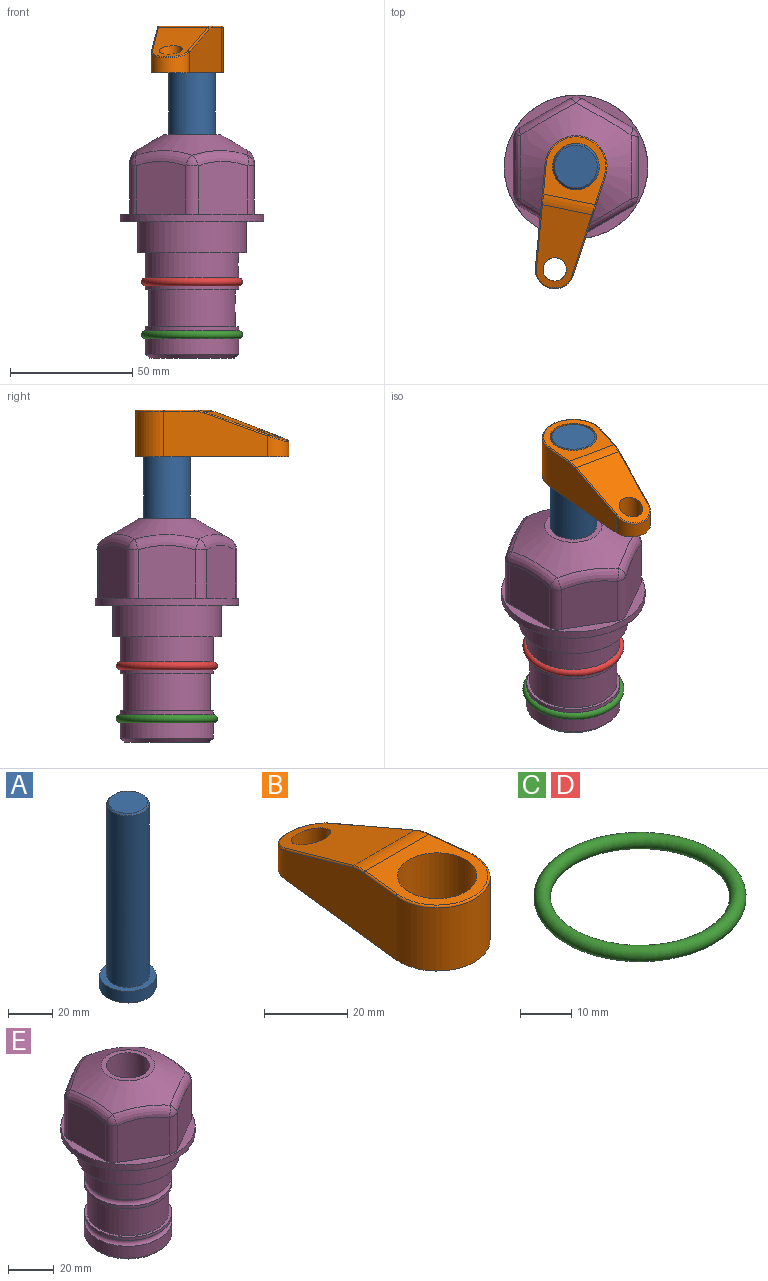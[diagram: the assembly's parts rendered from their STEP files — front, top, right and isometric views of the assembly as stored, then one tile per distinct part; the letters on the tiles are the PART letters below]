
ASSEMBLY  parts=5 mates=3
PART A: 6 faces, bbox 25.4x25.4x101.6 mm
  f0: plane 17.46x17.46mm, normal (0,0,1), area 239.5mm2, adj f5
  f1: plane 25.4x25.4mm, normal (0,0,-1), area 506.7mm2, adj f2
  f2: cylinder r=12.7mm len=25.4mm, axis (0,0,1), area 506.7mm2, adj f1,f3
  f3: plane 25.4x25.4mm, normal (0,0,1), area 221.7mm2, adj f2,f4
  f4: cylinder r=9.53mm len=94.46mm, axis (0,0,1), area 5653mm2, adj f3,f5
  f5: cone r=8.73mm half-angle=45deg, axis (0,0,-1), area 64.4mm2, adj f0,f4
PART B: 44 faces, bbox 27.5x64.5x19.1 mm
  f0: plane 2.3x0.95mm, normal (0,0,-1), area 1mm2, adj f25,f30,f34
  f1: plane 63.5x25.4mm, normal (0,0,-1), area 561.7mm2, adj f2,f3,f4,f5,f6,f7,f19,f20
  f2: cylinder r=12.7mm len=25.4mm, axis (0,0,-1), area 792.2mm2, adj f1,f3,f5,f13
  f3: plane 42.33x18.54mm, normal (0.99,0.11,0), area 647mm2, adj f1,f2,f4,f11,f12,f14
  f4: cylinder r=7.94mm len=15.78mm, axis (0,0,-1), area 158.6mm2, adj f1,f3,f5,f16
  f5: plane 42.33x18.54mm, normal (-0.99,0.11,0), area 647mm2, adj f1,f2,f4,f15,f17,f18
  f6: cylinder r=9.53mm len=19.05mm, axis (0,0,-1), area 1140.1mm2, adj f1,f8
  f7: cylinder r=4.76mm len=10.98mm, axis (0,0,-1), area 276.1mm2, adj f1,f9
  f8: plane 25.83x24.38mm, normal (0,0,1), area 262.2mm2, adj f6,f10,f11,f13,f15
  f9: plane 32.49x20.55mm, normal (0,0.34,0.94), area 489.9mm2, adj f7,f10,f14,f16,f18
  f10: cylinder r=12.7mm len=21.49mm, axis (-1,0,0), area 93.2mm2, adj f8,f9,f12,f17
  f11: cylinder r=0.51mm len=12.34mm, axis (0.11,-0.99,0), area 9.9mm2, adj f3,f8,f12,f13
  f12: bspline ~7.62x1.64mm, area 3.5mm2, adj f3,f10,f11,f14
  f13: torus R=12.19mm, axis (0,0,1), area 33.6mm2, adj f2,f8,f11,f15
  f14: cylinder r=0.51mm len=26.01mm, axis (0.1,-0.93,0.34), area 21.6mm2, adj f3,f9,f12,f16
  f15: cylinder r=0.51mm len=12.34mm, axis (0.11,0.99,0), area 9.9mm2, adj f5,f8,f13,f17
  f16: bspline ~15.78x7.05mm, area 15.7mm2, adj f4,f9,f14,f18
  f17: bspline ~7.62x1.64mm, area 3.5mm2, adj f5,f10,f15,f18
  f18: cylinder r=0.51mm len=26.01mm, axis (0.1,0.93,-0.34), area 21.6mm2, adj f5,f9,f16,f17
  f19: plane 21.6x14.29mm, normal (-0.99,-0.11,0), area 242.6mm2, adj f1,f26,f28,f34,f36,f38
  f20: plane 21.6x14.29mm, normal (0.99,-0.11,0), area 242.6mm2, adj f1,f27,f29,f37,f39,f41
  f21: cylinder r=12.7mm len=14.29mm, axis (0,0,-1), area 173.2mm2, adj f1,f26,f27,f30,f31,f33
  f22: cylinder r=7.94mm len=7.63mm, axis (0,0,-1), area 53.8mm2, adj f1,f28,f29,f42
  f23: plane 2.3x0.95mm, normal (0,0,-1), area 1mm2, adj f25,f33,f37
  f24: plane 17.94x12.32mm, normal (0,-0.34,-0.94), area 191.2mm2, adj f25,f38,f41,f42
  f25: cylinder r=9.53mm len=12.93mm, axis (-1,0,0), area 37.5mm2, adj f0,f23,f24,f31,f36,f39
  f26: cylinder r=1.59mm len=14.29mm, axis (0,0,-1), area 49mm2, adj f1,f19,f21,f32
  f27: cylinder r=1.59mm len=14.29mm, axis (0,0,-1), area 49mm2, adj f1,f20,f21,f35
  f28: cylinder r=1.59mm len=7.28mm, axis (0,0,-1), area 22.1mm2, adj f1,f19,f22,f40
  f29: cylinder r=1.59mm len=7.28mm, axis (0,0,-1), area 22.1mm2, adj f1,f20,f22,f43
  f30: torus R=14.29mm, axis (0,0,1), area 5.8mm2, adj f0,f21,f31,f32
  f31: bspline ~11.06x2.73mm, area 20.8mm2, adj f21,f25,f30,f33
  f32: sphere r=1.59mm, area 5.4mm2, adj f26,f30,f34
  f33: torus R=14.29mm, axis (0,0,1), area 5.8mm2, adj f21,f23,f31,f35
  f34: cylinder r=1.59mm len=1.68mm, axis (-0.11,0.99,0), area 2.4mm2, adj f0,f19,f32,f36
  f35: sphere r=1.59mm, area 5.4mm2, adj f27,f33,f37
  f36: bspline ~5.82x2.33mm, area 7.7mm2, adj f19,f25,f34,f38
  f37: cylinder r=1.59mm len=1.68mm, axis (0.11,0.99,0), area 2.4mm2, adj f20,f23,f35,f39
  f38: cylinder r=1.59mm len=18.33mm, axis (0.1,-0.93,0.34), area 46.7mm2, adj f19,f24,f36,f40
  f39: bspline ~5.82x2.33mm, area 7.7mm2, adj f20,f25,f37,f41
  f40: sphere r=1.59mm, area 3.6mm2, adj f28,f38,f42
  f41: cylinder r=1.59mm len=18.33mm, axis (0.1,0.93,-0.34), area 46.7mm2, adj f20,f24,f39,f43
  f42: bspline ~8.31x1.84mm, area 15.3mm2, adj f22,f24,f40,f43
  f43: sphere r=1.59mm, area 3.6mm2, adj f29,f41,f42
PART C: 1 faces, bbox 44.7x44.7x3.2 mm
  f0: torus R=19.05mm, axis (0,0,1), area 1193.9mm2
PART D: same geometry as C
PART E: 48 faces, bbox 58.7x60.9x91.2 mm
  f0: cylinder r=17.78mm len=35.56mm, axis (0,0,1), area 1670.8mm2, adj f23,f24,f31
  f1: cylinder r=19.05mm len=38.1mm, axis (0,0,1), area 1191.9mm2, adj f26,f27,f30
  f2: plane 58.66x58.66mm, normal (0,0,-1), area 1150.6mm2, adj f3,f28
  f3: cylinder r=29.33mm len=58.66mm, axis (0,0,-1), area 585.1mm2, adj f2,f4
  f4: plane 58.66x58.66mm, normal (0,0,1), area 475.9mm2, adj f3,f5,f6,f7,f8,f9,f10,f11
  f5: plane 21.57x20.33mm, normal (-0.5,0.87,0), area 491.3mm2, adj f4,f15,f16,f43
  f6: plane 21.57x20.33mm, normal (0.5,0.87,0), area 491.3mm2, adj f4,f14,f15,f39
  f7: plane 23.48x21.57mm, normal (1,0,0), area 491.3mm2, adj f4,f13,f14,f36
  f8: plane 21.57x20.33mm, normal (0.5,-0.87,0), area 491.3mm2, adj f4,f12,f13,f40
  f9: plane 21.57x20.33mm, normal (-0.5,-0.87,0), area 491.3mm2, adj f4,f11,f12,f44
  f10: plane 23.48x21.57mm, normal (-1,0,0), area 491.3mm2, adj f4,f11,f16,f47
  f11: cylinder r=5.08mm len=19.75mm, axis (0,0,-1), area 105mm2, adj f4,f9,f10,f46
  f12: cylinder r=5.08mm len=19.75mm, axis (0,0,-1), area 105mm2, adj f4,f8,f9,f42
  f13: cylinder r=5.08mm len=19.75mm, axis (0,0,-1), area 105mm2, adj f4,f7,f8,f38
  f14: cylinder r=5.08mm len=19.75mm, axis (0,0,-1), area 105mm2, adj f4,f6,f7,f37
  f15: cylinder r=5.08mm len=19.75mm, axis (0,0,-1), area 105mm2, adj f4,f5,f6,f41
  f16: cylinder r=5.08mm len=19.75mm, axis (0,0,-1), area 105mm2, adj f4,f5,f10,f45
  f17: cone r=11.73mm half-angle=60deg, axis (0,0,-1), area 1568.6mm2, adj f18,f36,f39,f40,f43,f44,f47
  f18: plane 23.46x23.46mm, normal (0,0,1), area 147.4mm2, adj f17,f35
  f19: plane 34.93x34.93mm, normal (0,0,-1), area 958mm2, adj f29
  f20: cylinder r=19.05mm len=38.1mm, axis (0,0,1), area 760.1mm2, adj f21,f29
  f21: torus R=19.05mm, axis (0,0,1), area 565.3mm2, adj f20,f22
  f22: cylinder r=19.05mm len=38.1mm, axis (0,0,1), area 190mm2, adj f21,f23
  f23: plane 38.1x38.1mm, normal (0,0,1), area 146.9mm2, adj f0,f22
  f24: plane 38.1x38.1mm, normal (0,0,-1), area 146.9mm2, adj f0,f25
  f25: cylinder r=19.05mm len=38.1mm, axis (0,0,1), area 190mm2, adj f24,f26
  f26: torus R=19.05mm, axis (0,0,1), area 565.3mm2, adj f1,f25
  f27: plane 44.45x44.45mm, normal (0,0,-1), area 411.7mm2, adj f1,f28
  f28: cylinder r=22.23mm len=44.45mm, axis (0,0,1), area 1773.5mm2, adj f2,f27
  f29: cone r=19.05mm half-angle=45deg, axis (0,0,1), area 257.5mm2, adj f19,f20
  f30: cylinder r=3.17mm len=6.75mm, axis (-1,0,0), area 128mm2, adj f1,f33
  f31: cylinder r=3.17mm len=6.35mm, axis (-1,0,0), area 102.5mm2, adj f0,f33
  f32: plane 25.4x25.4mm, normal (0,0,1), area 506.7mm2, adj f33
  f33: cylinder r=12.7mm len=66.42mm, axis (0,0,-1), area 5236.2mm2, adj f30,f31,f32,f34
  f34: cone r=9.53mm half-angle=30deg, axis (0,0,-1), area 443.4mm2, adj f33,f35
  f35: cylinder r=9.53mm len=19.05mm, axis (0,0,-1), area 849mm2, adj f18,f34
  f36: bspline ~34.65x7.53mm, area 137.7mm2, adj f7,f17,f37,f38
  f37: sphere r=5.08mm, area 15.9mm2, adj f14,f36,f39
  f38: sphere r=5.08mm, area 15.9mm2, adj f13,f36,f40
  f39: bspline ~31.16x19.76mm, area 137.7mm2, adj f6,f17,f37,f41
  f40: bspline ~28.3x18.17mm, area 137.7mm2, adj f8,f17,f38,f42
  f41: sphere r=5.08mm, area 15.4mm2, adj f15,f39,f43
  f42: sphere r=5.08mm, area 15.4mm2, adj f12,f40,f44
  f43: bspline ~31.16x19.76mm, area 137.7mm2, adj f5,f17,f41,f45
  f44: bspline ~31.16x19.76mm, area 137.7mm2, adj f9,f17,f42,f46
  f45: sphere r=5.08mm, area 15.9mm2, adj f16,f43,f47
  f46: sphere r=5.08mm, area 15.9mm2, adj f11,f44,f47
  f47: bspline ~31.43x7.53mm, area 137.7mm2, adj f10,f17,f45,f46
PLACE A rot(axis=(0,0,-1),101.7deg) t=(0,0,6.38)mm
PLACE B rot(axis=(0,0,1),168.3deg) t=(0,0,60.99)mm
PLACE C t=(0,0,-21.59)mm
PLACE D at identity
PLACE E at identity fixed
MATE fastened C.f0 <-> E.f0  axis (0,0,1) through (0,0,-46.1)mm
MATE cylindrical A.f2 <-> E.f0  axis (0,0,1) through (0,0,32.01)mm
MATE fastened B.f2 <-> A.f2  axis (0,0,1) through (0,0,80.04)mm
